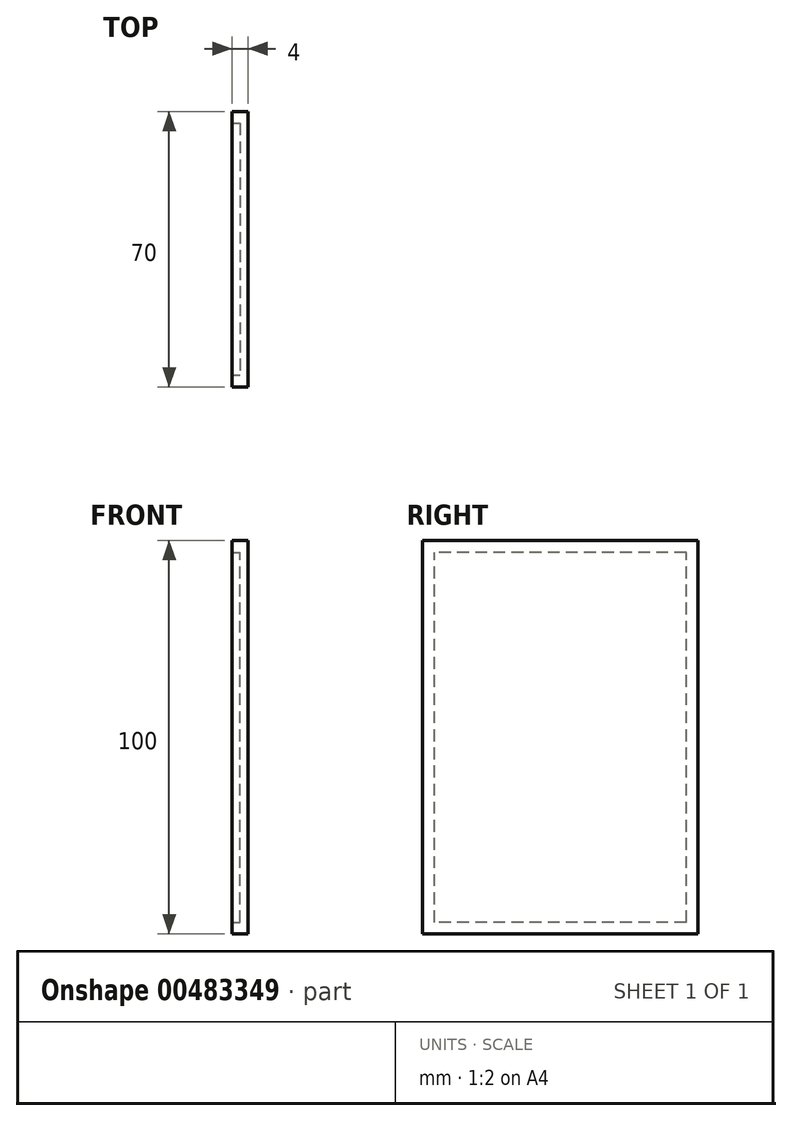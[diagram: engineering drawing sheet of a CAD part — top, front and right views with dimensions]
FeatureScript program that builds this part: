
annotation { "Feature Type Name" : "Feature", "Feature Type Description" : "" }
export const myFeature = defineFeature(function(context is Context, id is Id, definition is map)
    precondition{}
    {
        {
            var Q0;
            Q0=qCreatedBy(makeId("Right.planeOp"),FACE);
            var sketch = newSketch(context, id + "F0", { "sketchPlane" : qUnion([Q0])});
            skLineSegment(sketch, "E0.bottom", {"start": v(-35, 50) * mm, "end": v(35, 50) * mm});
            skLineSegment(sketch, "E0.top", {"start": v(-35, -50) * mm, "end": v(35, -50) * mm});
            skLineSegment(sketch, "E0.left", {"start": v(-35, 50) * mm, "end": v(-35, -50) * mm});
            skLineSegment(sketch, "E0.right", {"start": v(35, 50) * mm, "end": v(35, -50) * mm});
            skSolve(sketch);
        }
        {
            var Q0;
            Q0=makeQuery(id+"F0.imprint","IMPRINT",FACE,{"disambiguationData":[TD([[makeQuery(id+"F0.imprint","IMPRINT",EDGE,{"derivedFrom":sQuery(id+"F0.wireOp",EDGE,"E0.bottom")}),-1.0]])]});
            extrude(context, id + "F1", {"entities" : qUnion([Q0]), "depth" : 2 * mm});
        }
        {
            var Q0;
            Q0=makeQuery(id+"F1.opExtrude","CAP_FACE",FACE,{"disambiguationData":[OSD([sQuery(id+"F0.wireOp",EDGE,"E0.bottom"),sQuery(id+"F0.wireOp",EDGE,"E0.top"),sQuery(id+"F0.wireOp",EDGE,"E0.left"),sQuery(id+"F0.wireOp",EDGE,"E0.right")])],"isStart":true});
            var sketch = newSketch(context, id + "F2", { "sketchPlane" : qUnion([Q0])});
            skLineSegment(sketch, "E1.bottom", {"start": v(-32, -47) * mm, "end": v(32, -47) * mm});
            skLineSegment(sketch, "E1.top", {"start": v(-32, 47) * mm, "end": v(32, 47) * mm});
            skLineSegment(sketch, "E1.left", {"start": v(-32, -47) * mm, "end": v(-32, 47) * mm});
            skLineSegment(sketch, "E1.right", {"start": v(32, -47) * mm, "end": v(32, 47) * mm});
            skPoint(sketch, "E2.endSnap0", {"position": v(0, 47) * mm});
            skLineSegment(sketch, "E3", {"start": v(32, -6.5) * mm, "end": v(35, -6.5) * mm, "construction": true});
            skLineSegment(sketch, "E4", {"start": v(0, -47) * mm, "end": v(0, -50) * mm, "construction": true});
            skLineSegment(sketch, "E5", {"start": v(-35, -3) * mm, "end": v(-32, -3) * mm, "construction": true});
            skLineSegment(sketch, "E6", {"start": v(-2.92, 47) * mm, "end": v(-2.92, 50) * mm, "construction": true});
            skSolve(sketch);
        }
        {
            var Q0;
            Q0=makeQuery(id+"F2.imprint","IMPRINT",FACE,{"disambiguationData":[TD([[makeQuery(id+"F2.imprint","IMPRINT",EDGE,{"derivedFrom":sQuery(id+"F2.wireOp",EDGE,"E1.bottom")}),-1.0]])]});
            extrude(context, id + "F3", {"entities" : qUnion([Q0]), "operationType" : NewBodyOperationType.ADD, "depth" : 2 * mm});
        }
    });
